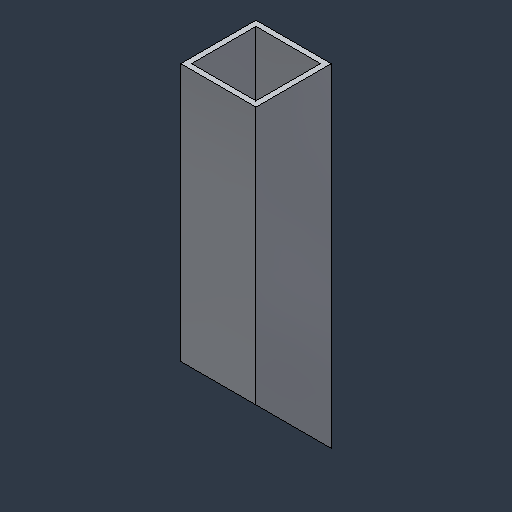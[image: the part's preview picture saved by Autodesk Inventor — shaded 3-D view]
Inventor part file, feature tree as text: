
AUTODESK INVENTOR PART (.ipt)
format: ipt  version: 2024.3 (Build 283343000, 343)  size: 83,456 bytes
history: native  units: mm (DEFAULTED — no unit token found)
features: chamfer x1
ambient origin geometry x8: Origin, YZ Plane, XZ Plane, XY Plane, X Axis, Y Axis, Z Axis, Center Point
bodies: Solid1 (feature_tree)
feature tree (1):
  chamfer  "Chamfer1"  [1 undecoded]
note: 1 required parameter value undecoded (feature->parameter linkage not recoverable at this tier; creation-order binding heuristic only, values carry confidence <= 0.55)
